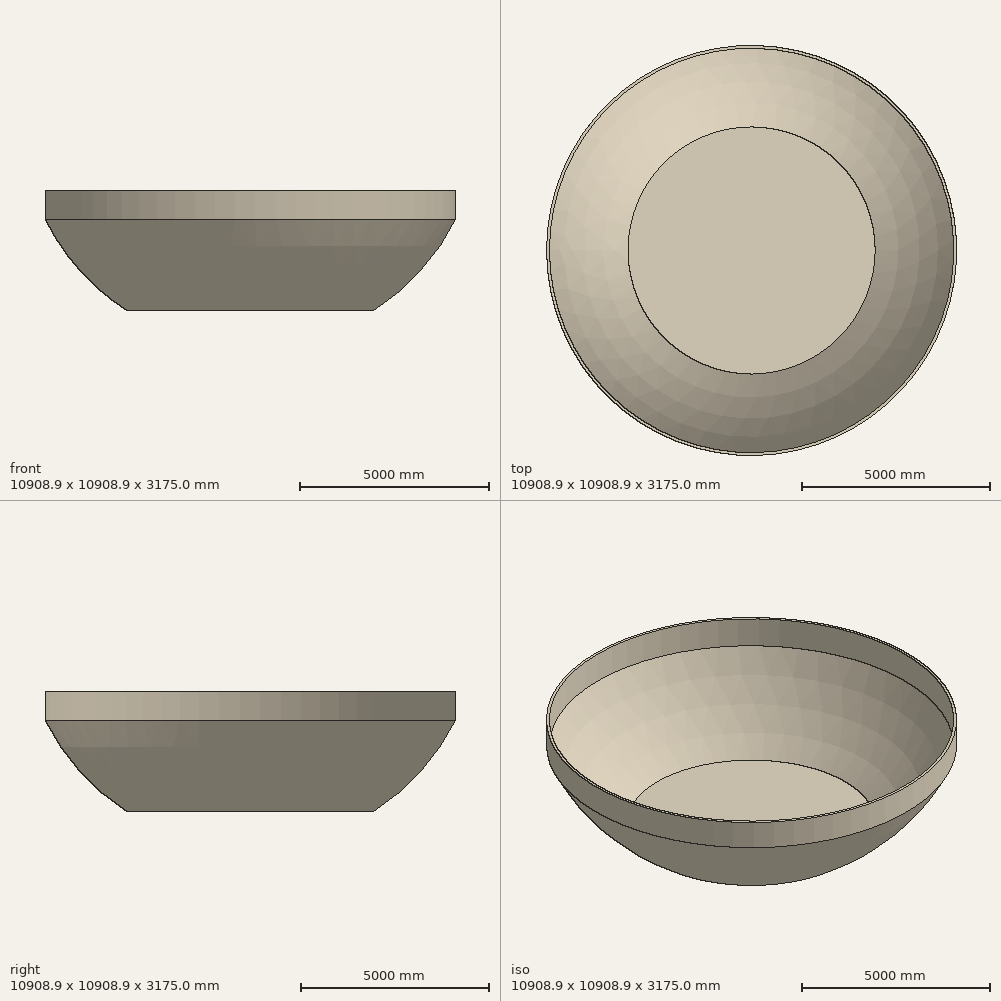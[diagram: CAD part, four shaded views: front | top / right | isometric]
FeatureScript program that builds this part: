
annotation { "Feature Type Name" : "Feature", "Feature Type Description" : "" }
export const myFeature = defineFeature(function(context is Context, id is Id, definition is map)
    precondition{}
    {
        {
            var Q0;
            Q0=qCreatedBy(makeId("Front.planeOp"),FACE);
            var sketch = newSketch(context, id + "F0", { "sketchPlane" : qUnion([Q0])});
            skLineSegment(sketch, "E0", {"start": v(0, 0) * mm, "end": v(-3302, 0) * mm});
            skLineSegment(sketch, "E1", {"start": v(-3287.01, 44.45) * mm, "end": v(0, 44.26) * mm});
            skLineSegment(sketch, "E2", {"start": v(0, 44.26) * mm, "end": v(0, 0) * mm});
            skLineSegment(sketch, "E3", {"start": v(0, 44.26) * mm, "end": v(0, 5311.51) * mm, "construction": true});
            skLineSegment(sketch, "E4", {"start": v(-900.7, 5124.26) * mm, "end": v(762.85, 5124.26) * mm, "construction": true});
            skArc(sketch, "E5", {"start": v(-3287.01, 44.45) * mm, "mid": v(-4483.03, 1060.84) * mm, "end": v(-5377.38, 2350.68) * mm});
            skArc(sketch, "E6", {"start": v(-3302, 0) * mm, "mid": v(-4539.98, 1056.12) * mm, "end": v(-5454.46, 2402.12) * mm});
            skLineSegment(sketch, "E7", {"start": v(-5454.46, 3175) * mm, "end": v(-5454.46, 2402.12) * mm});
            skLineSegment(sketch, "E8", {"start": v(-5377.38, 2350.68) * mm, "end": v(-5377.38, 3175) * mm});
            skLineSegment(sketch, "E9", {"start": v(-5454.46, 3175) * mm, "end": v(-5377.38, 3175) * mm});
            skSolve(sketch);
        }
        {
            var Q0;
            Q0 = qSketchRegion(id + "F0", true);
            var Q1;
            Q1=sQuery(id+"F0.wireOp",EDGE,"E3");
            revolve(context, id + "F1", {"entities" : qUnion([Q0]), "axis" : qUnion([Q1]), "revolveType" : RevolveType.FULL});
        }
    });
